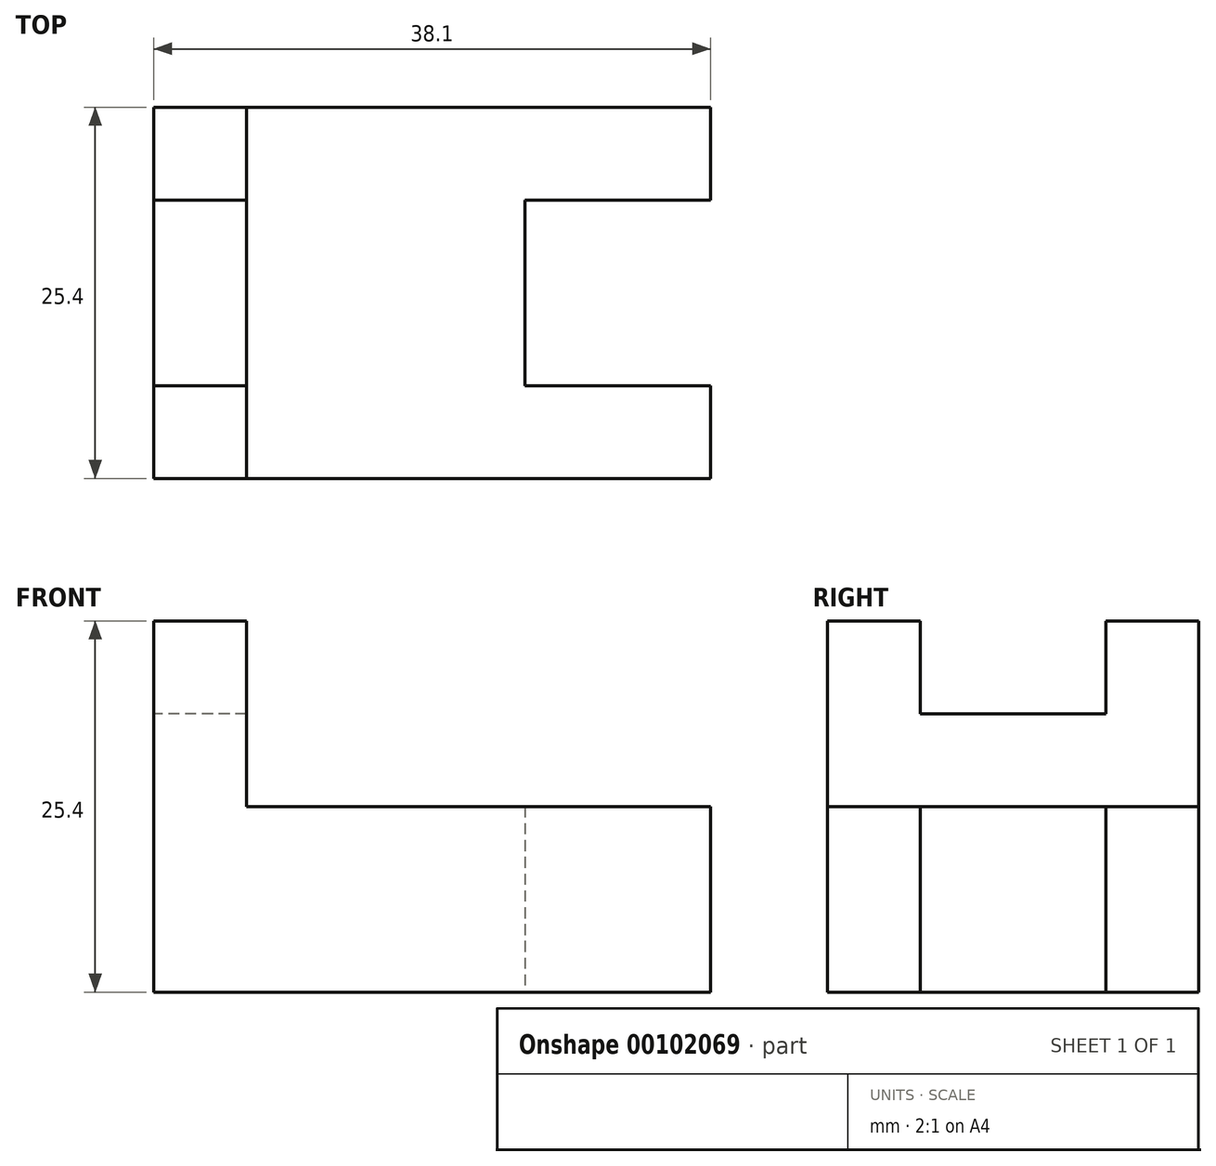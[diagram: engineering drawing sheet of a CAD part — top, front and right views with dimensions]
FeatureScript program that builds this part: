
annotation { "Feature Type Name" : "Feature", "Feature Type Description" : "" }
export const myFeature = defineFeature(function(context is Context, id is Id, definition is map)
    precondition{}
    {
        {
            var Q0;
            Q0=qCreatedBy(makeId("Front.planeOp"),FACE);
            var sketch = newSketch(context, id + "F0", { "sketchPlane" : qUnion([Q0])});
            skLineSegment(sketch, "E0", {"start": v(0, 0) * mm, "end": v(0, 25.4) * mm});
            skLineSegment(sketch, "E1", {"start": v(0, 25.4) * mm, "end": v(6.35, 25.4) * mm});
            skLineSegment(sketch, "E2", {"start": v(6.35, 25.4) * mm, "end": v(6.35, 12.7) * mm});
            skLineSegment(sketch, "E3", {"start": v(6.35, 12.7) * mm, "end": v(38.1, 12.7) * mm});
            skLineSegment(sketch, "E4", {"start": v(38.1, 12.7) * mm, "end": v(38.1, 0) * mm});
            skLineSegment(sketch, "E5", {"start": v(38.1, 0) * mm, "end": v(0, 0) * mm});
            skSolve(sketch);
        }
        {
            var Q0;
            Q0 = qSketchRegion(id + "F0", true);
            extrude(context, id + "F1", {"entities" : qUnion([Q0]), "endBound" : BoundingType.SYMMETRIC, "depth" : 25.4 * mm});
        }
        {
            var Q0;
            Q0=qCreatedBy(makeId("Right.planeOp"),FACE);
            var sketch = newSketch(context, id + "F2", { "sketchPlane" : qUnion([Q0])});
            skLineSegment(sketch, "E6", {"start": v(6.35, 25.4) * mm, "end": v(6.35, 19.05) * mm});
            skLineSegment(sketch, "E7", {"start": v(6.35, 19.05) * mm, "end": v(-6.35, 19.05) * mm});
            skLineSegment(sketch, "E8", {"start": v(-6.35, 19.05) * mm, "end": v(-6.35, 25.4) * mm});
            skLineSegment(sketch, "E9", {"start": v(-6.35, 25.4) * mm, "end": v(6.35, 25.4) * mm});
            skLineSegment(sketch, "E10", {"start": v(0, 0) * mm, "end": v(0, 25.4) * mm, "construction": true});
            skSolve(sketch);
        }
        {
            var Q0;
            Q0=makeQuery(id+"F2.imprint","IMPRINT",FACE,{"disambiguationData":[TD([[makeQuery(id+"F2.imprint","IMPRINT",EDGE,{"derivedFrom":sQuery(id+"F2.wireOp",EDGE,"E6")}),-1.0]])]});
            extrude(context, id + "F3", {"entities" : qUnion([Q0]), "operationType" : NewBodyOperationType.REMOVE, "endBound" : BoundingType.THROUGH_ALL, "depth" : 25.4 * mm});
        }
        {
            var Q0;
            Q0=qCreatedBy(makeId("Top.planeOp"),FACE);
            var sketch = newSketch(context, id + "F4", { "sketchPlane" : qUnion([Q0])});
            skLineSegment(sketch, "E11", {"start": v(38.1, -6.35) * mm, "end": v(25.4, -6.35) * mm});
            skLineSegment(sketch, "E12", {"start": v(25.4, -6.35) * mm, "end": v(25.4, 6.35) * mm});
            skLineSegment(sketch, "E13", {"start": v(25.4, 6.35) * mm, "end": v(38.1, 6.35) * mm});
            skLineSegment(sketch, "E14", {"start": v(38.1, 6.35) * mm, "end": v(38.1, -6.35) * mm});
            skSolve(sketch);
        }
        {
            var Q0;
            Q0=makeQuery(id+"F4.imprint","IMPRINT",FACE,{"disambiguationData":[TD([[makeQuery(id+"F4.imprint","IMPRINT",EDGE,{"derivedFrom":sQuery(id+"F4.wireOp",EDGE,"E11")}),-1.0]])]});
            extrude(context, id + "F5", {"entities" : qUnion([Q0]), "operationType" : NewBodyOperationType.REMOVE, "endBound" : BoundingType.THROUGH_ALL, "depth" : 25.4 * mm});
        }
    });
